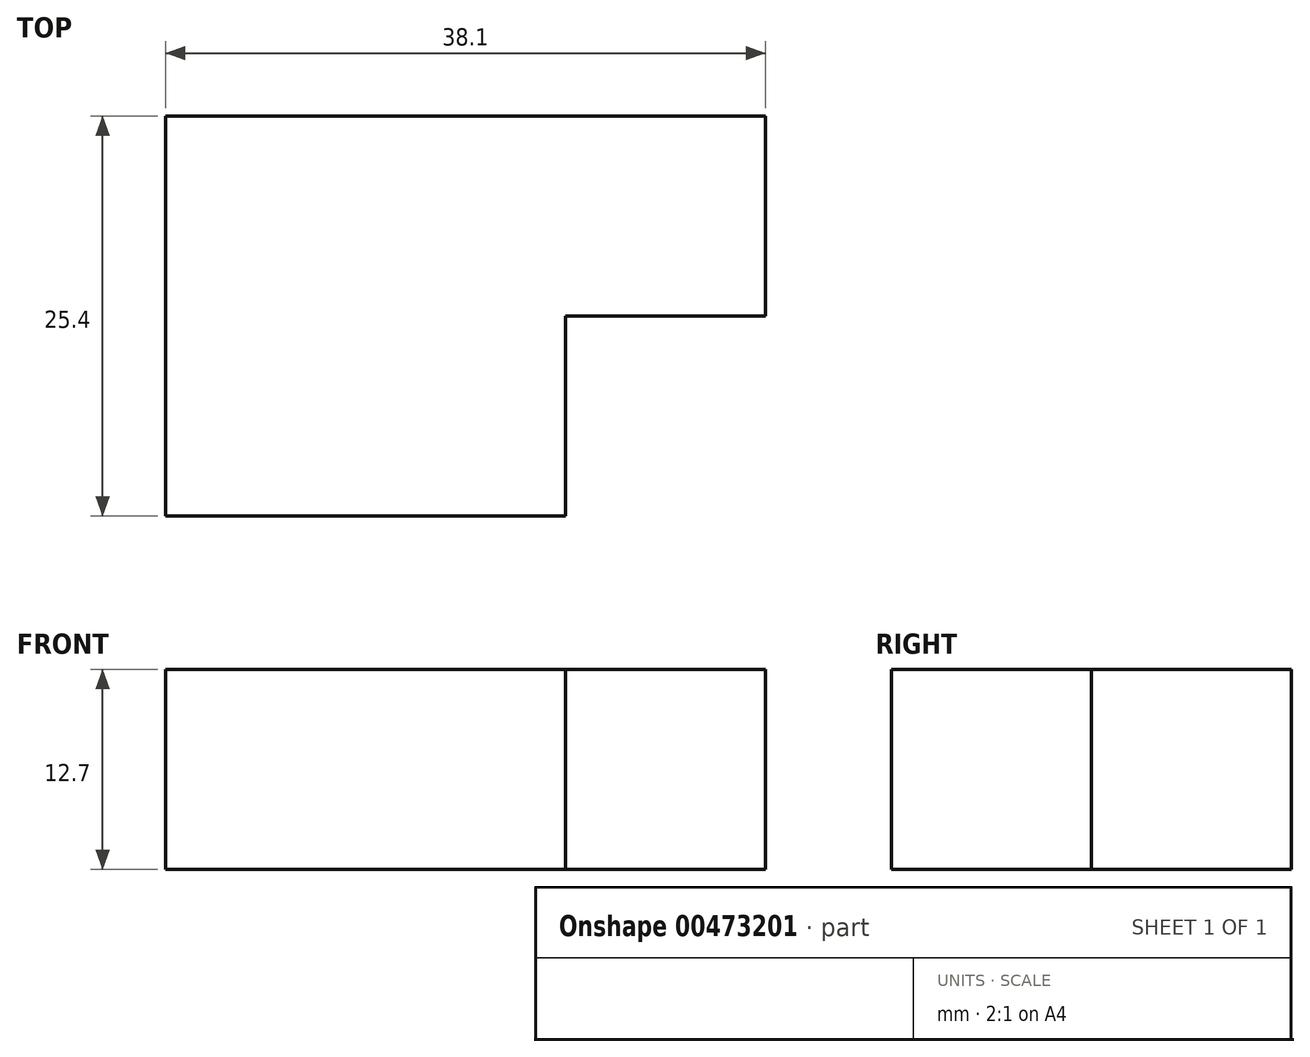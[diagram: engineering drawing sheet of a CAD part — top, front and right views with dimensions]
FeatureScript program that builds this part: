
annotation { "Feature Type Name" : "Feature", "Feature Type Description" : "" }
export const myFeature = defineFeature(function(context is Context, id is Id, definition is map)
    precondition{}
    {
        {
            var Q0;
            Q0=qCreatedBy(makeId("Top.planeOp"),FACE);
            var sketch = newSketch(context, id + "F0", { "sketchPlane" : qUnion([Q0])});
            skLineSegment(sketch, "E0", {"start": v(32.68, -18.36) * mm, "end": v(7.28, -18.36) * mm});
            skLineSegment(sketch, "E1", {"start": v(7.28, -18.36) * mm, "end": v(7.28, 7.04) * mm});
            skLineSegment(sketch, "E2", {"start": v(7.28, 7.04) * mm, "end": v(45.38, 7.04) * mm});
            skLineSegment(sketch, "E3", {"start": v(45.38, 7.04) * mm, "end": v(45.38, -5.66) * mm});
            skLineSegment(sketch, "E4", {"start": v(45.38, -5.66) * mm, "end": v(32.68, -5.66) * mm});
            skLineSegment(sketch, "E5", {"start": v(32.68, -5.66) * mm, "end": v(32.68, -18.36) * mm});
            skSolve(sketch);
        }
        {
            var Q0;
            Q0 = qSketchRegion(id + "F0", true);
            extrude(context, id + "F1", {"entities" : qUnion([Q0]), "depth" : 12.7 * mm});
        }
    });
